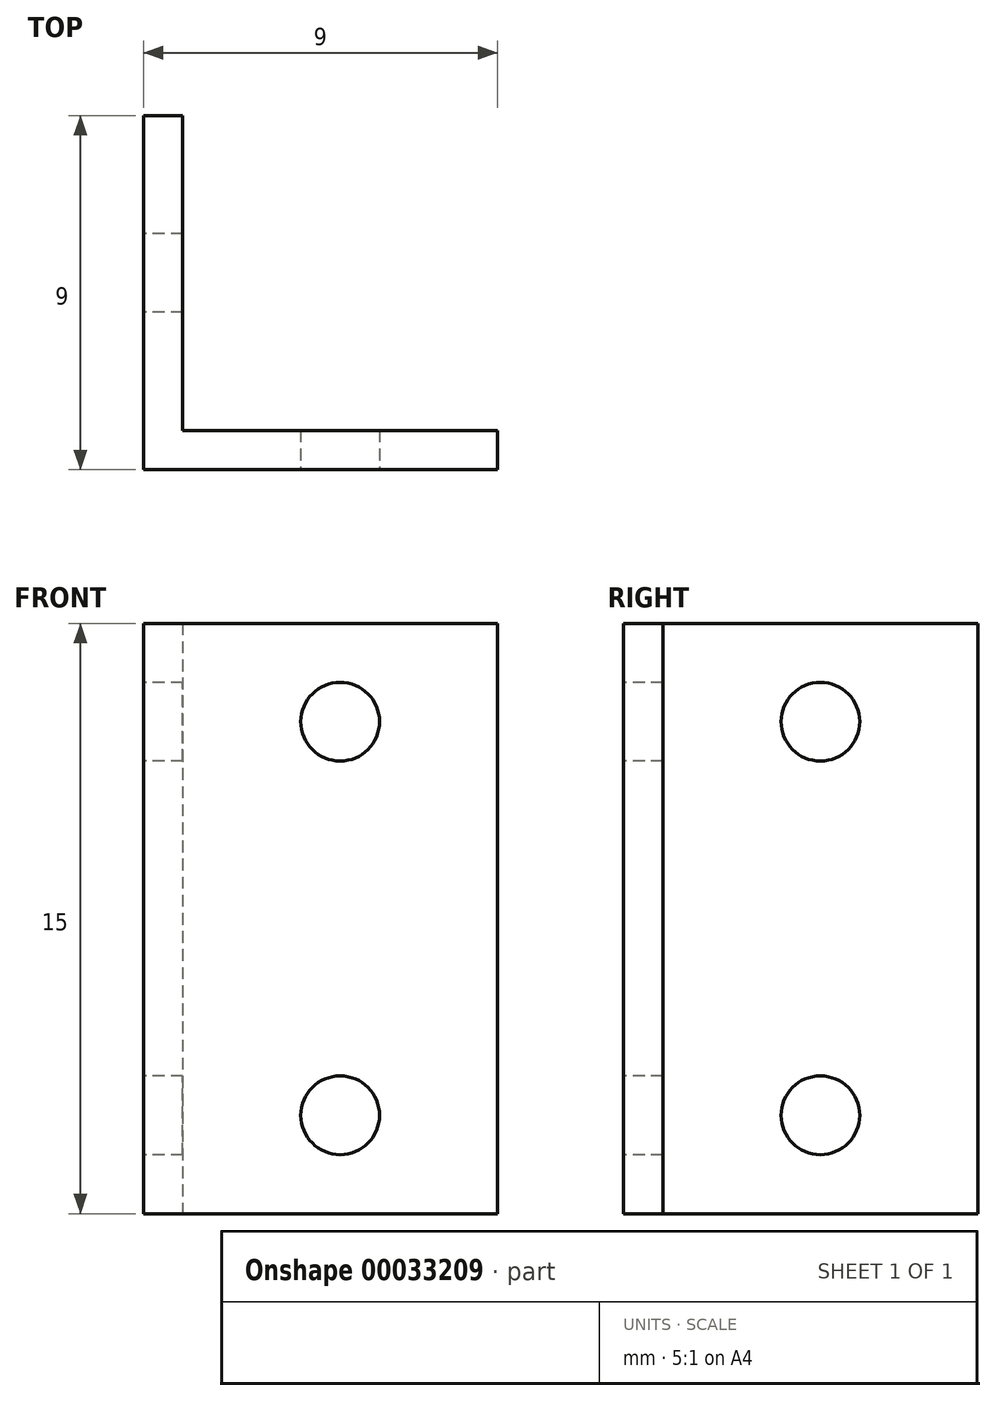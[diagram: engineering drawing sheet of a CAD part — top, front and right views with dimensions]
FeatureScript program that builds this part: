
annotation { "Feature Type Name" : "Feature", "Feature Type Description" : "" }
export const myFeature = defineFeature(function(context is Context, id is Id, definition is map)
    precondition{}
    {
        {
            var Q0;
            Q0=qCreatedBy(makeId("Top.planeOp"),FACE);
            var sketch = newSketch(context, id + "F0", { "sketchPlane" : qUnion([Q0])});
            skLineSegment(sketch, "E0.bottom", {"start": v(0, 0) * mm, "end": v(9, 0) * mm});
            skLineSegment(sketch, "E0.top", {"start": v(0, 9) * mm, "end": v(1, 9) * mm});
            skLineSegment(sketch, "E0.left", {"start": v(0, 0) * mm, "end": v(0, 9) * mm});
            skLineSegment(sketch, "E0.right", {"start": v(9, 0) * mm, "end": v(9, 1) * mm});
            skLineSegment(sketch, "E1.top", {"start": v(9, 1) * mm, "end": v(1, 1) * mm});
            skLineSegment(sketch, "E1.right", {"start": v(1, 9) * mm, "end": v(1, 1) * mm});
            skSolve(sketch);
        }
        {
            var Q0;
            Q0 = qSketchRegion(id + "F0", true);
            extrude(context, id + "F1", {"entities" : qUnion([Q0]), "depth" : 15 * mm});
        }
        {
            var Q0;
            Q0=makeQuery(id+"F1.opExtrude","SWEPT_FACE",FACE,{"disambiguationData":[OSD([sQuery(id+"F0.wireOp",EDGE,"E0.bottom")])]});
            var sketch = newSketch(context, id + "F2", { "sketchPlane" : qUnion([Q0])});
            skLineSegment(sketch, "E2", {"start": v(0, 7.5) * mm, "end": v(9, 7.5) * mm, "construction": true});
            skCircle(sketch, "E3", {"center": v(5, 12.5) * mm, "radius": 1 * mm});
            skCircle(sketch, "E4.MirrorC", {"center": v(5, 2.5) * mm, "radius": 1 * mm});
            skSolve(sketch);
        }
        {
            var Q0;
            Q0 = qSketchRegion(id + "F2", true);
            extrude(context, id + "F3", {"entities" : qUnion([Q0]), "operationType" : NewBodyOperationType.REMOVE, "endBound" : BoundingType.UP_TO_NEXT, "oppositeDirection" : true, "depth" : 25 * mm});
        }
        {
            var Q0;
            Q0=makeQuery(id+"F1.opExtrude","SWEPT_FACE",FACE,{"disambiguationData":[OSD([sQuery(id+"F0.wireOp",EDGE,"E0.left")])]});
            var sketch = newSketch(context, id + "F4", { "sketchPlane" : qUnion([Q0])});
            skLineSegment(sketch, "E5", {"start": v(-9, 7.5) * mm, "end": v(0, 7.5) * mm, "construction": true});
            skCircle(sketch, "E6", {"center": v(-5, 12.5) * mm, "radius": 1 * mm});
            skCircle(sketch, "E7.MirrorC", {"center": v(-5, 2.5) * mm, "radius": 1 * mm});
            skSolve(sketch);
        }
        {
            var Q0;
            Q0 = qSketchRegion(id + "F4", true);
            extrude(context, id + "F5", {"entities" : qUnion([Q0]), "operationType" : NewBodyOperationType.REMOVE, "endBound" : BoundingType.UP_TO_NEXT, "oppositeDirection" : true, "depth" : 25 * mm});
        }
    });
